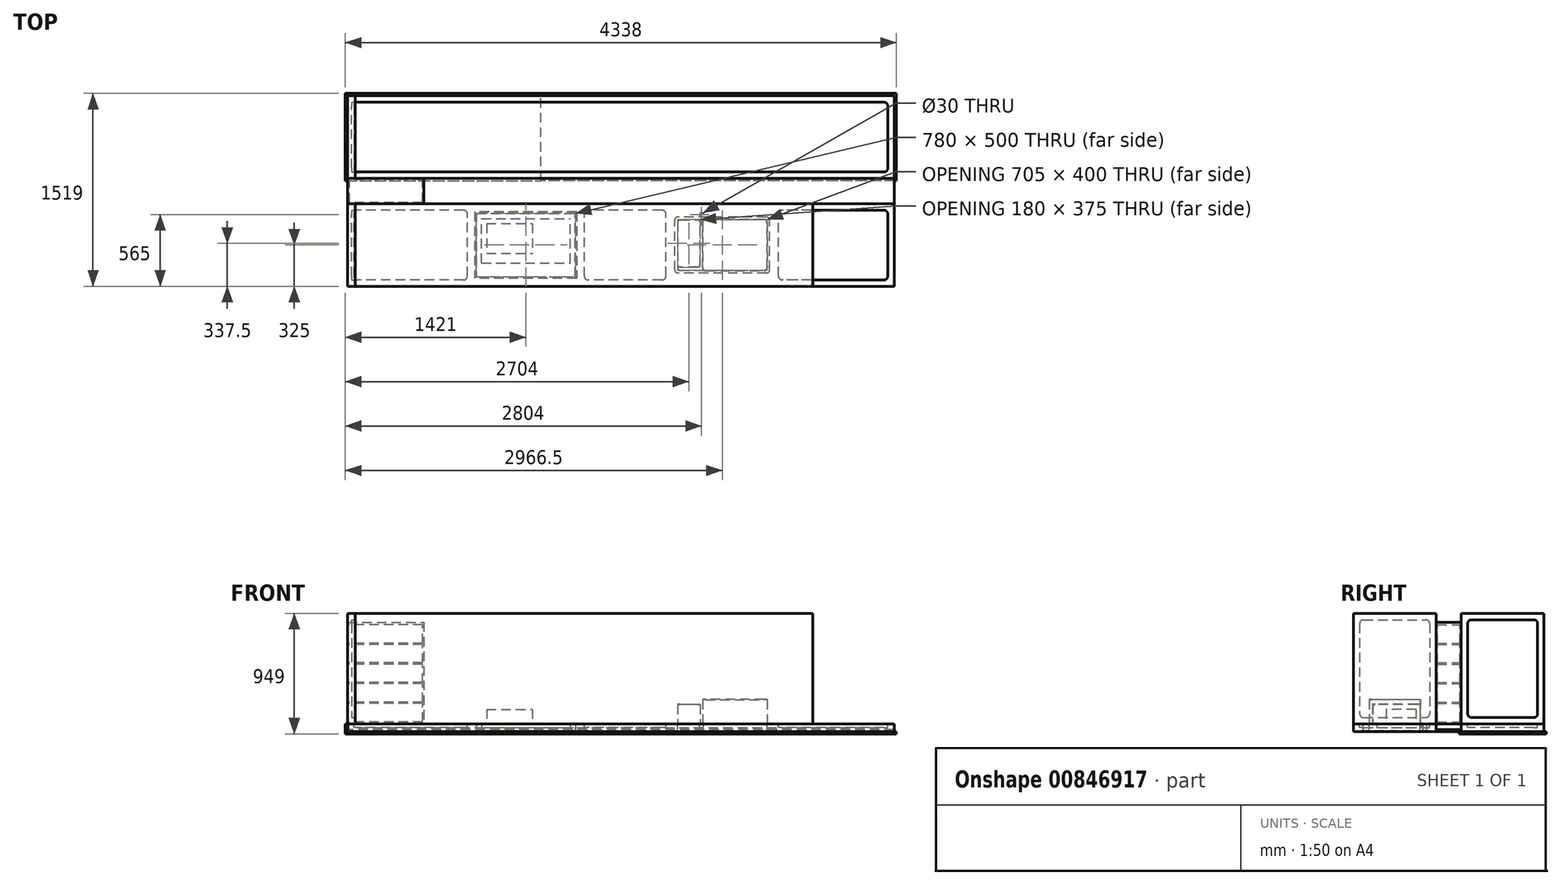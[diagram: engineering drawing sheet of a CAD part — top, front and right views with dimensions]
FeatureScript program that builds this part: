
annotation { "Feature Type Name" : "Feature", "Feature Type Description" : "" }
export const myFeature = defineFeature(function(context is Context, id is Id, definition is map)
    precondition{}
    {
        {
            var Q0;
            Q0=qCreatedBy(makeId("Top.planeOp"),FACE);
            var sketch = newSketch(context, id + "F0", { "sketchPlane" : qUnion([Q0])});
            skLineSegment(sketch, "E0.bottom", {"start": v(0, 0) * mm, "end": v(4300, 0) * mm});
            skLineSegment(sketch, "E0.top", {"start": v(0, 650) * mm, "end": v(4300, 650) * mm});
            skLineSegment(sketch, "E0.left", {"start": v(0, 0) * mm, "end": v(0, 650) * mm});
            skLineSegment(sketch, "E0.right", {"start": v(4300, 0) * mm, "end": v(4300, 650) * mm});
            skSolve(sketch);
        }
        {
            var Q0;
            Q0=makeQuery(id+"F0.imprint","IMPRINT",FACE,{"disambiguationData":[TD([[makeQuery(id+"F0.imprint","IMPRINT",EDGE,{"derivedFrom":sQuery(id+"F0.wireOp",EDGE,"E0.bottom")}),1.0]])]});
            extrude(context, id + "F1", {"entities" : qUnion([Q0]), "depth" : 60 * mm, "offsetDistance" : 25 * mm});
        }
        {
            var Q0;
            Q0=makeQuery(id+"F1.opExtrude","CAP_FACE",FACE,{"disambiguationData":[OSD([sQuery(id+"F0.wireOp",EDGE,"E0.bottom"),sQuery(id+"F0.wireOp",EDGE,"E0.top"),sQuery(id+"F0.wireOp",EDGE,"E0.left"),sQuery(id+"F0.wireOp",EDGE,"E0.right")])],"isStart":false});
            var sketch = newSketch(context, id + "F2", { "sketchPlane" : qUnion([Q0])});
            skLineSegment(sketch, "E1.bottom", {"start": v(2617, 525) * mm, "end": v(3278, 525) * mm});
            skLineSegment(sketch, "E1.top", {"start": v(2617, 125) * mm, "end": v(3278, 125) * mm});
            skLineSegment(sketch, "E1.left", {"start": v(2595, 503) * mm, "end": v(2595, 147) * mm});
            skLineSegment(sketch, "E1.right", {"start": v(3300, 503) * mm, "end": v(3300, 147) * mm});
            skPoint(sketch, "E2.visualSharp", {"position": v(2595, 525) * mm});
            skArc(sketch, "E2.filletArc", {"start": v(2617, 525) * mm, "mid": v(2601.44, 518.56) * mm, "end": v(2595, 503) * mm});
            skPoint(sketch, "E3.visualSharp", {"position": v(3300, 525) * mm});
            skArc(sketch, "E3.filletArc", {"start": v(3300, 503) * mm, "mid": v(3293.56, 518.56) * mm, "end": v(3278, 525) * mm});
            skPoint(sketch, "E4.visualSharp", {"position": v(3300, 125) * mm});
            skArc(sketch, "E4.filletArc", {"start": v(3278, 125) * mm, "mid": v(3293.56, 131.44) * mm, "end": v(3300, 147) * mm});
            skPoint(sketch, "E5.visualSharp", {"position": v(2595, 125) * mm});
            skArc(sketch, "E5.filletArc", {"start": v(2595, 147) * mm, "mid": v(2601.44, 131.44) * mm, "end": v(2617, 125) * mm});
            skCircle(sketch, "E6", {"center": v(2785, 565) * mm, "radius": 15 * mm});
            skSolve(sketch);
        }
        {
            var Q0;
            Q0 = qSketchRegion(id + "F2", true);
            extrude(context, id + "F3", {"entities" : qUnion([Q0]), "operationType" : NewBodyOperationType.REMOVE, "endBound" : BoundingType.THROUGH_ALL, "oppositeDirection" : true, "depth" : 25 * mm, "offsetDistance" : 25 * mm});
        }
        {
            var Q0;
            Q0=makeQuery(id+"F1.opExtrude","CAP_FACE",FACE,{"disambiguationData":[OSD([sQuery(id+"F0.wireOp",EDGE,"E0.bottom"),sQuery(id+"F0.wireOp",EDGE,"E0.top"),sQuery(id+"F0.wireOp",EDGE,"E0.left"),sQuery(id+"F0.wireOp",EDGE,"E0.right")])],"isStart":false});
            var sketch = newSketch(context, id + "F4", { "sketchPlane" : qUnion([Q0])});
            skLineSegment(sketch, "E7.bottom", {"start": v(3298, 105) * mm, "end": v(2597, 105) * mm});
            skLineSegment(sketch, "E7.top", {"start": v(3298, 545) * mm, "end": v(2597, 545) * mm});
            skLineSegment(sketch, "E7.left", {"start": v(3320, 127) * mm, "end": v(3320, 523) * mm});
            skLineSegment(sketch, "E7.right", {"start": v(2575, 127) * mm, "end": v(2575, 523) * mm});
            skPoint(sketch, "E8.visualSharp", {"position": v(2575, 105) * mm});
            skArc(sketch, "E8.filletArc", {"start": v(2575, 127) * mm, "mid": v(2581.44, 111.44) * mm, "end": v(2597, 105) * mm});
            skPoint(sketch, "E9.visualSharp", {"position": v(2575, 545) * mm});
            skArc(sketch, "E9.filletArc", {"start": v(2597, 545) * mm, "mid": v(2581.44, 538.56) * mm, "end": v(2575, 523) * mm});
            skPoint(sketch, "E10.visualSharp", {"position": v(3320, 545) * mm});
            skArc(sketch, "E10.filletArc", {"start": v(3320, 523) * mm, "mid": v(3313.56, 538.56) * mm, "end": v(3298, 545) * mm});
            skPoint(sketch, "E11.visualSharp", {"position": v(3320, 105) * mm});
            skArc(sketch, "E11.filletArc", {"start": v(3298, 105) * mm, "mid": v(3313.56, 111.44) * mm, "end": v(3320, 127) * mm});
            skLineSegment(sketch, "E12.left", {"start": v(2795, 147) * mm, "end": v(2795, 503) * mm});
            skLineSegment(sketch, "E12.right", {"start": v(2775, 172) * mm, "end": v(2775, 503) * mm});
            skLineSegment(sketch, "E13.bottom", {"start": v(2817, 125) * mm, "end": v(3278, 125) * mm});
            skLineSegment(sketch, "E13.top", {"start": v(2817, 525) * mm, "end": v(3278, 525) * mm});
            skLineSegment(sketch, "E13.right", {"start": v(3300, 147) * mm, "end": v(3300, 503) * mm});
            skPoint(sketch, "E14.visualSharp", {"position": v(2795, 125) * mm});
            skArc(sketch, "E14.filletArc", {"start": v(2795, 147) * mm, "mid": v(2801.44, 131.44) * mm, "end": v(2817, 125) * mm});
            skPoint(sketch, "E15.visualSharp", {"position": v(3300, 125) * mm});
            skArc(sketch, "E15.filletArc", {"start": v(3278, 125) * mm, "mid": v(3293.56, 131.44) * mm, "end": v(3300, 147) * mm});
            skPoint(sketch, "E16.visualSharp", {"position": v(3300, 525) * mm});
            skArc(sketch, "E16.filletArc", {"start": v(3300, 503) * mm, "mid": v(3293.56, 518.56) * mm, "end": v(3278, 525) * mm});
            skPoint(sketch, "E17.visualSharp", {"position": v(2795, 525) * mm});
            skArc(sketch, "E17.filletArc", {"start": v(2817, 525) * mm, "mid": v(2801.44, 518.56) * mm, "end": v(2795, 503) * mm});
            skLineSegment(sketch, "E18.bottom", {"start": v(2753, 150) * mm, "end": v(2617, 150) * mm});
            skLineSegment(sketch, "E18.top", {"start": v(2753, 525) * mm, "end": v(2617, 525) * mm});
            skLineSegment(sketch, "E18.right", {"start": v(2595, 172) * mm, "end": v(2595, 503) * mm});
            skPoint(sketch, "E19.visualSharp", {"position": v(2775, 150) * mm});
            skArc(sketch, "E19.filletArc", {"start": v(2753, 150) * mm, "mid": v(2768.56, 156.44) * mm, "end": v(2775, 172) * mm});
            skPoint(sketch, "E20.visualSharp", {"position": v(2595, 525) * mm});
            skArc(sketch, "E20.filletArc", {"start": v(2617, 525) * mm, "mid": v(2601.44, 518.56) * mm, "end": v(2595, 503) * mm});
            skPoint(sketch, "E21.visualSharp", {"position": v(2775, 525) * mm});
            skArc(sketch, "E21.filletArc", {"start": v(2775, 503) * mm, "mid": v(2768.56, 518.56) * mm, "end": v(2753, 525) * mm});
            skPoint(sketch, "E22.visualSharp", {"position": v(2595, 150) * mm});
            skArc(sketch, "E22.filletArc", {"start": v(2595, 172) * mm, "mid": v(2601.44, 156.44) * mm, "end": v(2617, 150) * mm});
            skSolve(sketch);
        }
        {
            var Q0;
            Q0 = qSketchRegion(id + "F4", true);
            extrude(context, id + "F5", {"entities" : qUnion([Q0]), "depth" : 2 * mm, "offsetDistance" : 25 * mm});
        }
        {
            var Q0;
            Q0=makeQuery(id+"F5.opExtrude","CAP_FACE",FACE,{"disambiguationData":[OSD([sQuery(id+"F4.wireOp",EDGE,"E7.bottom"),sQuery(id+"F4.wireOp",EDGE,"E7.top"),sQuery(id+"F4.wireOp",EDGE,"E7.left"),sQuery(id+"F4.wireOp",EDGE,"E7.right"),sQuery(id+"F4.wireOp",EDGE,"E8.filletArc"),sQuery(id+"F4.wireOp",EDGE,"E9.filletArc"),sQuery(id+"F4.wireOp",EDGE,"E10.filletArc"),sQuery(id+"F4.wireOp",EDGE,"E11.filletArc"),sQuery(id+"F4.wireOp",EDGE,"E13.bottom"),sQuery(id+"F4.wireOp",EDGE,"E13.top"),sQuery(id+"F4.wireOp",EDGE,"E12.left"),sQuery(id+"F4.wireOp",EDGE,"E13.right"),sQuery(id+"F4.wireOp",EDGE,"E14.filletArc"),sQuery(id+"F4.wireOp",EDGE,"E15.filletArc"),sQuery(id+"F4.wireOp",EDGE,"E16.filletArc"),sQuery(id+"F4.wireOp",EDGE,"E17.filletArc"),sQuery(id+"F4.wireOp",EDGE,"E18.bottom"),sQuery(id+"F4.wireOp",EDGE,"E18.top"),sQuery(id+"F4.wireOp",EDGE,"E12.right"),sQuery(id+"F4.wireOp",EDGE,"E18.right"),sQuery(id+"F4.wireOp",EDGE,"E19.filletArc"),sQuery(id+"F4.wireOp",EDGE,"E20.filletArc"),sQuery(id+"F4.wireOp",EDGE,"E21.filletArc"),sQuery(id+"F4.wireOp",EDGE,"E22.filletArc")])],"isStart":false});
            var sketch = newSketch(context, id + "F6", { "sketchPlane" : qUnion([Q0])});
            skLineSegment(sketch, "E23.0.0", {"start": v(3278, 525) * mm, "end": v(2817, 525) * mm});
            skArc(sketch, "E23.0.1", {"start": v(2817, 525) * mm, "mid": v(2801.44, 518.56) * mm, "end": v(2795, 503) * mm});
            skLineSegment(sketch, "E23.0.2", {"start": v(2795, 503) * mm, "end": v(2795, 147) * mm});
            skArc(sketch, "E23.0.3", {"start": v(2795, 147) * mm, "mid": v(2801.44, 131.44) * mm, "end": v(2817, 125) * mm});
            skLineSegment(sketch, "E23.0.4", {"start": v(2817, 125) * mm, "end": v(3278, 125) * mm});
            skArc(sketch, "E23.0.5", {"start": v(3278, 125) * mm, "mid": v(3293.56, 131.44) * mm, "end": v(3300, 147) * mm});
            skLineSegment(sketch, "E23.0.6", {"start": v(3300, 147) * mm, "end": v(3300, 503) * mm});
            skArc(sketch, "E23.0.7", {"start": v(3300, 503) * mm, "mid": v(3293.56, 518.56) * mm, "end": v(3278, 525) * mm});
            skArc(sketch, "E24.0", {"start": v(3302, 503) * mm, "mid": v(3294.97, 519.97) * mm, "end": v(3278, 527) * mm});
            skLineSegment(sketch, "E24.1", {"start": v(3302, 147) * mm, "end": v(3302, 503) * mm});
            skLineSegment(sketch, "E24.2", {"start": v(3278, 527) * mm, "end": v(2817, 527) * mm});
            skArc(sketch, "E24.3", {"start": v(3278, 123) * mm, "mid": v(3294.97, 130.03) * mm, "end": v(3302, 147) * mm});
            skArc(sketch, "E24.4", {"start": v(2817, 527) * mm, "mid": v(2800.03, 519.97) * mm, "end": v(2793, 503) * mm});
            skLineSegment(sketch, "E24.5", {"start": v(2793, 503) * mm, "end": v(2793, 147) * mm});
            skArc(sketch, "E24.6", {"start": v(2793, 147) * mm, "mid": v(2800.03, 130.03) * mm, "end": v(2817, 123) * mm});
            skLineSegment(sketch, "E24.7", {"start": v(2817, 123) * mm, "end": v(3278, 123) * mm});
            skSolve(sketch);
        }
        {
            var Q0;
            Q0 = qSketchRegion(id + "F6", true);
            extrude(context, id + "F7", {"entities" : qUnion([Q0]), "operationType" : NewBodyOperationType.ADD, "depth" : 190 * mm, "offsetDistance" : 25 * mm});
        }
        {
            var Q0;
            Q0=makeQuery(id+"F7.opExtrude","CAP_FACE",FACE,{"disambiguationData":[OSD([sQuery(id+"F6.wireOp",EDGE,"E23.0.0"),sQuery(id+"F6.wireOp",EDGE,"E23.0.1"),sQuery(id+"F6.wireOp",EDGE,"E23.0.2"),sQuery(id+"F6.wireOp",EDGE,"E23.0.3"),sQuery(id+"F6.wireOp",EDGE,"E23.0.4"),sQuery(id+"F6.wireOp",EDGE,"E23.0.5"),sQuery(id+"F6.wireOp",EDGE,"E23.0.6"),sQuery(id+"F6.wireOp",EDGE,"E23.0.7"),sQuery(id+"F6.wireOp",EDGE,"E24.0"),sQuery(id+"F6.wireOp",EDGE,"E24.1"),sQuery(id+"F6.wireOp",EDGE,"E24.2"),sQuery(id+"F6.wireOp",EDGE,"E24.3"),sQuery(id+"F6.wireOp",EDGE,"E24.4"),sQuery(id+"F6.wireOp",EDGE,"E24.5"),sQuery(id+"F6.wireOp",EDGE,"E24.6"),sQuery(id+"F6.wireOp",EDGE,"E24.7")])],"isStart":false});
            var sketch = newSketch(context, id + "F8", { "sketchPlane" : qUnion([Q0])});
            skLineSegment(sketch, "E25.0.0", {"start": v(3278, 525) * mm, "end": v(2817, 525) * mm});
            skArc(sketch, "E25.0.1", {"start": v(2817, 525) * mm, "mid": v(2801.44, 518.56) * mm, "end": v(2795, 503) * mm});
            skLineSegment(sketch, "E25.0.2", {"start": v(2795, 503) * mm, "end": v(2795, 147) * mm});
            skArc(sketch, "E25.0.3", {"start": v(2795, 147) * mm, "mid": v(2801.44, 131.44) * mm, "end": v(2817, 125) * mm});
            skLineSegment(sketch, "E25.0.4", {"start": v(2817, 125) * mm, "end": v(3278, 125) * mm});
            skArc(sketch, "E25.0.5", {"start": v(3278, 125) * mm, "mid": v(3293.56, 131.44) * mm, "end": v(3300, 147) * mm});
            skLineSegment(sketch, "E25.0.6", {"start": v(3300, 147) * mm, "end": v(3300, 503) * mm});
            skArc(sketch, "E25.0.7", {"start": v(3300, 503) * mm, "mid": v(3293.56, 518.56) * mm, "end": v(3278, 525) * mm});
            skSolve(sketch);
        }
        {
            var Q0;
            Q0 = qSketchRegion(id + "F8", true);
            extrude(context, id + "F9", {"entities" : qUnion([Q0]), "operationType" : NewBodyOperationType.ADD, "oppositeDirection" : true, "depth" : 2 * mm, "offsetDistance" : 25 * mm});
        }
        {
            var Q0;
            Q0=makeQuery(id+"F5.opExtrude","CAP_FACE",FACE,{"disambiguationData":[OSD([sQuery(id+"F4.wireOp",EDGE,"E7.bottom"),sQuery(id+"F4.wireOp",EDGE,"E7.top"),sQuery(id+"F4.wireOp",EDGE,"E7.left"),sQuery(id+"F4.wireOp",EDGE,"E7.right"),sQuery(id+"F4.wireOp",EDGE,"E8.filletArc"),sQuery(id+"F4.wireOp",EDGE,"E9.filletArc"),sQuery(id+"F4.wireOp",EDGE,"E10.filletArc"),sQuery(id+"F4.wireOp",EDGE,"E11.filletArc"),sQuery(id+"F4.wireOp",EDGE,"E13.bottom"),sQuery(id+"F4.wireOp",EDGE,"E13.top"),sQuery(id+"F4.wireOp",EDGE,"E12.left"),sQuery(id+"F4.wireOp",EDGE,"E13.right"),sQuery(id+"F4.wireOp",EDGE,"E14.filletArc"),sQuery(id+"F4.wireOp",EDGE,"E15.filletArc"),sQuery(id+"F4.wireOp",EDGE,"E16.filletArc"),sQuery(id+"F4.wireOp",EDGE,"E17.filletArc"),sQuery(id+"F4.wireOp",EDGE,"E18.bottom"),sQuery(id+"F4.wireOp",EDGE,"E18.top"),sQuery(id+"F4.wireOp",EDGE,"E12.right"),sQuery(id+"F4.wireOp",EDGE,"E18.right"),sQuery(id+"F4.wireOp",EDGE,"E19.filletArc"),sQuery(id+"F4.wireOp",EDGE,"E20.filletArc"),sQuery(id+"F4.wireOp",EDGE,"E21.filletArc"),sQuery(id+"F4.wireOp",EDGE,"E22.filletArc")])],"isStart":false});
            var sketch = newSketch(context, id + "F10", { "sketchPlane" : qUnion([Q0])});
            skLineSegment(sketch, "E26.0", {"start": v(2753, 152) * mm, "end": v(2617, 152) * mm});
            skArc(sketch, "E26.1", {"start": v(2597, 172) * mm, "mid": v(2602.86, 157.86) * mm, "end": v(2617, 152) * mm});
            skArc(sketch, "E26.2", {"start": v(2753, 152) * mm, "mid": v(2767.14, 157.86) * mm, "end": v(2773, 172) * mm});
            skLineSegment(sketch, "E26.3", {"start": v(2597, 503) * mm, "end": v(2597, 172) * mm});
            skLineSegment(sketch, "E26.4", {"start": v(2773, 172) * mm, "end": v(2773, 503) * mm});
            skArc(sketch, "E26.5", {"start": v(2773, 503) * mm, "mid": v(2767.14, 517.14) * mm, "end": v(2753, 523) * mm});
            skLineSegment(sketch, "E26.6", {"start": v(2617, 523) * mm, "end": v(2753, 523) * mm});
            skArc(sketch, "E26.7", {"start": v(2617, 523) * mm, "mid": v(2602.86, 517.14) * mm, "end": v(2597, 503) * mm});
            skArc(sketch, "E27.0", {"start": v(2595, 172) * mm, "mid": v(2601.44, 156.44) * mm, "end": v(2617, 150) * mm});
            skLineSegment(sketch, "E28.0", {"start": v(2753, 150) * mm, "end": v(2617, 150) * mm});
            skArc(sketch, "E29.0", {"start": v(2753, 150) * mm, "mid": v(2768.56, 156.44) * mm, "end": v(2775, 172) * mm});
            skLineSegment(sketch, "E30.0", {"start": v(2775, 172) * mm, "end": v(2775, 503) * mm});
            skArc(sketch, "E31.0", {"start": v(2775, 503) * mm, "mid": v(2768.56, 518.56) * mm, "end": v(2753, 525) * mm});
            skLineSegment(sketch, "E32.0", {"start": v(2617, 525) * mm, "end": v(2753, 525) * mm});
            skArc(sketch, "E33.0", {"start": v(2617, 525) * mm, "mid": v(2601.44, 518.56) * mm, "end": v(2595, 503) * mm});
            skLineSegment(sketch, "E34.0", {"start": v(2595, 503) * mm, "end": v(2595, 172) * mm});
            skSolve(sketch);
        }
        {
            var Q0;
            Q0=makeQuery(id+"F10.imprint","IMPRINT",FACE,{"disambiguationData":[TD([[makeQuery(id+"F10.imprint","IMPRINT",EDGE,{"derivedFrom":sQuery(id+"F10.wireOp",EDGE,"E26.0")}),1.0]])]});
            extrude(context, id + "F11", {"entities" : qUnion([Q0]), "operationType" : NewBodyOperationType.ADD, "depth" : 150 * mm, "offsetDistance" : 25 * mm});
        }
        {
            var Q0;
            {var subQ0=sQuery(id+"F0.wireOp",EDGE,"E0.bottom");var subQ1=sQuery(id+"F0.wireOp",EDGE,"E0.left");var subQ2=sQuery(id+"F0.wireOp",EDGE,"E0.right");Q0=makeQuery(id+"F5oApF7oSFTbvsd_1.boolean.opBoolean","SPLIT",FACE,{"disambiguationData":[TD([makeQuery(id+"F1.opExtrude","SWEPT_FACE",FACE,{"disambiguationData":[OSD([subQ0])]})])],"derivedFrom":makeQuery(id+"F1.opExtrude","CAP_FACE",FACE,{"disambiguationData":[OSD([subQ0,sQuery(id+"F0.wireOp",EDGE,"E0.top"),subQ1,subQ2])],"isStart":true})});}
            var sketch = newSketch(context, id + "F12", { "sketchPlane" : qUnion([Q0])});
            skLineSegment(sketch, "E35.bottom", {"start": v(1804, -587) * mm, "end": v(1000, -587) * mm});
            skLineSegment(sketch, "E35.top", {"start": v(1804, -63) * mm, "end": v(1000, -63) * mm});
            skLineSegment(sketch, "E35.left", {"start": v(1804, -587) * mm, "end": v(1804, -63) * mm});
            skLineSegment(sketch, "E35.right", {"start": v(1000, -587) * mm, "end": v(1000, -63) * mm});
            skSolve(sketch);
        }
        {
            var Q0;
            Q0=makeQuery(id+"F12.imprint","IMPRINT",FACE,{"disambiguationData":[TD([[makeQuery(id+"F12.imprint","IMPRINT",EDGE,{"derivedFrom":sQuery(id+"F12.wireOp",EDGE,"E35.bottom")}),-1.0]])]});
            extrude(context, id + "F13", {"entities" : qUnion([Q0]), "operationType" : NewBodyOperationType.REMOVE, "oppositeDirection" : true, "depth" : 5 * mm, "offsetDistance" : 25 * mm});
        }
        {
            var Q0;
            Q0=makeQuery(id+"F13.boolean.opBoolean","COPY",FACE,{"derivedFrom":makeQuery(id+"F13.opExtrude","CAP_FACE",FACE,{"disambiguationData":[OSD([sQuery(id+"F12.wireOp",EDGE,"E35.bottom"),sQuery(id+"F12.wireOp",EDGE,"E35.top"),sQuery(id+"F12.wireOp",EDGE,"E35.left"),sQuery(id+"F12.wireOp",EDGE,"E35.right")])],"isStart":false})});
            var sketch = newSketch(context, id + "F14", { "sketchPlane" : qUnion([Q0])});
            skLineSegment(sketch, "E36.0", {"start": v(1792, -575) * mm, "end": v(1792, -75) * mm});
            skLineSegment(sketch, "E36.1", {"start": v(1012, -575) * mm, "end": v(1792, -575) * mm});
            skLineSegment(sketch, "E36.2", {"start": v(1012, -75) * mm, "end": v(1012, -575) * mm});
            skLineSegment(sketch, "E36.3", {"start": v(1792, -75) * mm, "end": v(1012, -75) * mm});
            skSolve(sketch);
        }
        {
            var Q0;
            Q0=makeQuery(id+"F14.imprint","IMPRINT",FACE,{"disambiguationData":[TD([[makeQuery(id+"F14.imprint","IMPRINT",EDGE,{"derivedFrom":sQuery(id+"F14.wireOp",EDGE,"E36.0")}),1.0]])]});
            extrude(context, id + "F15", {"entities" : qUnion([Q0]), "operationType" : NewBodyOperationType.REMOVE, "endBound" : BoundingType.THROUGH_ALL, "oppositeDirection" : true, "depth" : 25 * mm, "offsetDistance" : 25 * mm});
        }
        {
            var Q0;
            {var subQ0=sQuery(id+"F0.wireOp",EDGE,"E0.bottom");var subQ1=sQuery(id+"F0.wireOp",EDGE,"E0.left");var subQ2=sQuery(id+"F0.wireOp",EDGE,"E0.right");Q0=makeQuery(id+"F5oApF7oSFTbvsd_1.boolean.opBoolean","SPLIT",FACE,{"disambiguationData":[TD([makeQuery(id+"F1.opExtrude","SWEPT_FACE",FACE,{"disambiguationData":[OSD([subQ0])]})])],"derivedFrom":makeQuery(id+"F1.opExtrude","CAP_FACE",FACE,{"disambiguationData":[OSD([subQ0,sQuery(id+"F0.wireOp",EDGE,"E0.top"),subQ1,subQ2])],"isStart":true})});}
            var sketch = newSketch(context, id + "F16", { "sketchPlane" : qUnion([Q0])});
            skLineSegment(sketch, "E37.bottom", {"start": v(1802, -585) * mm, "end": v(1002, -585) * mm});
            skLineSegment(sketch, "E37.top", {"start": v(1802, -65) * mm, "end": v(1002, -65) * mm});
            skLineSegment(sketch, "E37.left", {"start": v(1802, -585) * mm, "end": v(1802, -65) * mm});
            skLineSegment(sketch, "E37.right", {"start": v(1002, -585) * mm, "end": v(1002, -65) * mm});
            skSolve(sketch);
        }
        {
            var Q0;
            Q0 = qSketchRegion(id + "F16", true);
            extrude(context, id + "F17", {"entities" : qUnion([Q0]), "oppositeDirection" : true, "depth" : 5 * mm, "offsetDistance" : 25 * mm});
        }
        {
            var Q0;
            Q0=makeQuery(id+"F17.opExtrude","CAP_FACE",FACE,{"disambiguationData":[OSD([sQuery(id+"F16.wireOp",EDGE,"E37.bottom"),sQuery(id+"F16.wireOp",EDGE,"E37.top"),sQuery(id+"F16.wireOp",EDGE,"E37.left"),sQuery(id+"F16.wireOp",EDGE,"E37.right")])],"isStart":false});
            var sketch = newSketch(context, id + "F18", { "sketchPlane" : qUnion([Q0])});
            skLineSegment(sketch, "E38.bottom", {"start": v(1013.5, 76.5) * mm, "end": v(1790.5, 76.5) * mm});
            skLineSegment(sketch, "E38.top", {"start": v(1013.5, 573.5) * mm, "end": v(1790.5, 573.5) * mm});
            skLineSegment(sketch, "E38.left", {"start": v(1013.5, 76.5) * mm, "end": v(1013.5, 573.5) * mm});
            skLineSegment(sketch, "E38.right", {"start": v(1790.5, 76.5) * mm, "end": v(1790.5, 573.5) * mm});
            skLineSegment(sketch, "E39", {"start": v(1121.78, 65) * mm, "end": v(1121.78, 76.5) * mm, "construction": true});
            skLineSegment(sketch, "E40", {"start": v(1128.6, 573.5) * mm, "end": v(1128.6, 585) * mm, "construction": true});
            skLineSegment(sketch, "E41", {"start": v(1002, 297.1) * mm, "end": v(1013.5, 297.1) * mm, "construction": true});
            skLineSegment(sketch, "E42", {"start": v(1802, 255.84) * mm, "end": v(1790.5, 255.84) * mm, "construction": true});
            skSolve(sketch);
        }
        {
            var Q0;
            Q0=makeQuery(id+"F18.imprint","IMPRINT",FACE,{"disambiguationData":[TD([[makeQuery(id+"F18.imprint","IMPRINT",EDGE,{"derivedFrom":sQuery(id+"F18.wireOp",EDGE,"E38.bottom")}),1.0]])]});
            extrude(context, id + "F19", {"entities" : qUnion([Q0]), "operationType" : NewBodyOperationType.ADD, "depth" : 25 * mm, "offsetDistance" : 25 * mm});
        }
        {
            var Q0;
            Q0=makeQuery(id+"F19.opExtrude","CAP_FACE",FACE,{"disambiguationData":[OSD([sQuery(id+"F18.wireOp",EDGE,"E38.bottom"),sQuery(id+"F18.wireOp",EDGE,"E38.top"),sQuery(id+"F18.wireOp",EDGE,"E38.left"),sQuery(id+"F18.wireOp",EDGE,"E38.right")])],"isStart":false});
            var sketch = newSketch(context, id + "F20", { "sketchPlane" : qUnion([Q0])});
            skLineSegment(sketch, "E43.bottom", {"start": v(1053.5, 183.5) * mm, "end": v(1753.5, 183.5) * mm});
            skLineSegment(sketch, "E43.top", {"start": v(1053.5, 533.5) * mm, "end": v(1753.5, 533.5) * mm});
            skLineSegment(sketch, "E43.left", {"start": v(1053.5, 183.5) * mm, "end": v(1053.5, 533.5) * mm});
            skLineSegment(sketch, "E43.right", {"start": v(1753.5, 183.5) * mm, "end": v(1753.5, 533.5) * mm});
            skSolve(sketch);
        }
        {
            var Q0;
            Q0=makeQuery(id+"F20.imprint","IMPRINT",FACE,{"disambiguationData":[TD([[makeQuery(id+"F20.imprint","IMPRINT",EDGE,{"derivedFrom":sQuery(id+"F20.wireOp",EDGE,"E43.bottom")}),1.0]])]});
            extrude(context, id + "F21", {"entities" : qUnion([Q0]), "operationType" : NewBodyOperationType.ADD, "depth" : 25 * mm, "offsetDistance" : 25 * mm});
        }
        {
            var Q0;
            Q0=makeQuery(id+"F21.opExtrude","CAP_FACE",FACE,{"disambiguationData":[OSD([sQuery(id+"F20.wireOp",EDGE,"E43.bottom"),sQuery(id+"F20.wireOp",EDGE,"E43.top"),sQuery(id+"F20.wireOp",EDGE,"E43.left"),sQuery(id+"F20.wireOp",EDGE,"E43.right")])],"isStart":false});
            var sketch = newSketch(context, id + "F22", { "sketchPlane" : qUnion([Q0])});
            skLineSegment(sketch, "E44.bottom", {"start": v(1093.5, 493.5) * mm, "end": v(1453.5, 493.5) * mm});
            skLineSegment(sketch, "E44.top", {"start": v(1093.5, 258.5) * mm, "end": v(1453.5, 258.5) * mm});
            skLineSegment(sketch, "E44.left", {"start": v(1093.5, 493.5) * mm, "end": v(1093.5, 258.5) * mm});
            skLineSegment(sketch, "E44.right", {"start": v(1453.5, 493.5) * mm, "end": v(1453.5, 258.5) * mm});
            skSolve(sketch);
        }
        {
            var Q0;
            Q0=makeQuery(id+"F22.imprint","IMPRINT",FACE,{"disambiguationData":[TD([[makeQuery(id+"F22.imprint","IMPRINT",EDGE,{"derivedFrom":sQuery(id+"F22.wireOp",EDGE,"E44.bottom")}),-1.0]])]});
            extrude(context, id + "F23", {"entities" : qUnion([Q0]), "operationType" : NewBodyOperationType.ADD, "depth" : 120 * mm, "offsetDistance" : 25 * mm});
        }
        {
            var Q0;
            Q0=makeQuery(id+"F11.opExtrude","CAP_FACE",FACE,{"disambiguationData":[OSD([sQuery(id+"F10.wireOp",EDGE,"E26.0"),sQuery(id+"F10.wireOp",EDGE,"E26.1"),sQuery(id+"F10.wireOp",EDGE,"E26.2"),sQuery(id+"F10.wireOp",EDGE,"E26.3"),sQuery(id+"F10.wireOp",EDGE,"E26.4"),sQuery(id+"F10.wireOp",EDGE,"E26.5"),sQuery(id+"F10.wireOp",EDGE,"E26.6"),sQuery(id+"F10.wireOp",EDGE,"E26.7"),sQuery(id+"F10.wireOp",EDGE,"E27.0"),sQuery(id+"F10.wireOp",EDGE,"E28.0"),sQuery(id+"F10.wireOp",EDGE,"E29.0"),sQuery(id+"F10.wireOp",EDGE,"E30.0"),sQuery(id+"F10.wireOp",EDGE,"E31.0"),sQuery(id+"F10.wireOp",EDGE,"E32.0"),sQuery(id+"F10.wireOp",EDGE,"E33.0"),sQuery(id+"F10.wireOp",EDGE,"E34.0")])],"isStart":false});
            var sketch = newSketch(context, id + "F24", { "sketchPlane" : qUnion([Q0])});
            skSolve(sketch);
        }
        {
            var Q0;
            Q0=makeQuery(id+"F24.imprint","IMPRINT",FACE,{"disambiguationData":[TD([[makeQuery(id+"F24.imprint","IMPRINT",EDGE,{"derivedFrom":makeQuery(id+"F11.opExtrude","CAP_EDGE",EDGE,{"disambiguationData":[OSD([sQuery(id+"F10.wireOp",EDGE,"E26.0")])],"isStart":false})}),1.0]])]});
            var sketch = newSketch(context, id + "F25", { "sketchPlane" : qUnion([Q0])});
            skArc(sketch, "E45.0", {"start": v(2753, 150) * mm, "mid": v(2768.56, 156.44) * mm, "end": v(2775, 172) * mm});
            skLineSegment(sketch, "E46.0", {"start": v(2775, 172) * mm, "end": v(2775, 503) * mm});
            skArc(sketch, "E47.0", {"start": v(2775, 503) * mm, "mid": v(2768.56, 518.56) * mm, "end": v(2753, 525) * mm});
            skLineSegment(sketch, "E48.0", {"start": v(2617, 525) * mm, "end": v(2753, 525) * mm});
            skArc(sketch, "E49.0", {"start": v(2617, 525) * mm, "mid": v(2601.44, 518.56) * mm, "end": v(2595, 503) * mm});
            skLineSegment(sketch, "E50.0", {"start": v(2595, 503) * mm, "end": v(2595, 172) * mm});
            skArc(sketch, "E51.0", {"start": v(2595, 172) * mm, "mid": v(2601.44, 156.44) * mm, "end": v(2617, 150) * mm});
            skLineSegment(sketch, "E52.0", {"start": v(2753, 150) * mm, "end": v(2617, 150) * mm});
            skSolve(sketch);
        }
        {
            var Q0;
            Q0 = qSketchRegion(id + "F25", true);
            extrude(context, id + "F26", {"entities" : qUnion([Q0]), "operationType" : NewBodyOperationType.ADD, "depth" : 2 * mm, "offsetDistance" : 25 * mm});
        }
        {
            var Q0;
            Q0=makeQuery(id+"F1.opExtrude","CAP_FACE",FACE,{"disambiguationData":[OSD([sQuery(id+"F0.wireOp",EDGE,"E0.bottom"),sQuery(id+"F0.wireOp",EDGE,"E0.top"),sQuery(id+"F0.wireOp",EDGE,"E0.left"),sQuery(id+"F0.wireOp",EDGE,"E0.right")])],"isStart":false});
            var sketch = newSketch(context, id + "F27", { "sketchPlane" : qUnion([Q0])});
            skLineSegment(sketch, "E53.bottom", {"start": v(4220, 50) * mm, "end": v(3420, 50) * mm});
            skLineSegment(sketch, "E53.top", {"start": v(4220, 600) * mm, "end": v(3420, 600) * mm});
            skLineSegment(sketch, "E53.left", {"start": v(4250, 80) * mm, "end": v(4250, 570) * mm});
            skLineSegment(sketch, "E53.right", {"start": v(3390, 80) * mm, "end": v(3390, 570) * mm});
            skLineSegment(sketch, "E54.bottom", {"start": v(2475, 50) * mm, "end": v(1892, 50) * mm});
            skLineSegment(sketch, "E54.top", {"start": v(2475, 600) * mm, "end": v(1892, 600) * mm});
            skLineSegment(sketch, "E54.left", {"start": v(2505, 80) * mm, "end": v(2505, 570) * mm});
            skLineSegment(sketch, "E54.right", {"start": v(1862, 80) * mm, "end": v(1862, 570) * mm});
            skLineSegment(sketch, "E55.bottom", {"start": v(912, 50) * mm, "end": v(80, 50) * mm});
            skLineSegment(sketch, "E55.top", {"start": v(912, 600) * mm, "end": v(80, 600) * mm});
            skLineSegment(sketch, "E55.left", {"start": v(942, 80) * mm, "end": v(942, 570) * mm});
            skLineSegment(sketch, "E55.right", {"start": v(50, 80) * mm, "end": v(50, 570) * mm});
            skPoint(sketch, "E56.visualSharp", {"position": v(50, 600) * mm});
            skArc(sketch, "E56.filletArc", {"start": v(80, 600) * mm, "mid": v(58.79, 591.21) * mm, "end": v(50, 570) * mm});
            skPoint(sketch, "E57.visualSharp", {"position": v(942, 600) * mm});
            skArc(sketch, "E57.filletArc", {"start": v(942, 570) * mm, "mid": v(933.21, 591.21) * mm, "end": v(912, 600) * mm});
            skPoint(sketch, "E58.visualSharp", {"position": v(942, 50) * mm});
            skArc(sketch, "E58.filletArc", {"start": v(912, 50) * mm, "mid": v(933.21, 58.79) * mm, "end": v(942, 80) * mm});
            skPoint(sketch, "E59.visualSharp", {"position": v(50, 50) * mm});
            skArc(sketch, "E59.filletArc", {"start": v(50, 80) * mm, "mid": v(58.79, 58.79) * mm, "end": v(80, 50) * mm});
            skPoint(sketch, "E60.visualSharp", {"position": v(1862, 600) * mm});
            skArc(sketch, "E60.filletArc", {"start": v(1892, 600) * mm, "mid": v(1870.79, 591.21) * mm, "end": v(1862, 570) * mm});
            skPoint(sketch, "E61.visualSharp", {"position": v(2505, 600) * mm});
            skArc(sketch, "E61.filletArc", {"start": v(2505, 570) * mm, "mid": v(2496.21, 591.21) * mm, "end": v(2475, 600) * mm});
            skPoint(sketch, "E62.visualSharp", {"position": v(2505, 50) * mm});
            skArc(sketch, "E62.filletArc", {"start": v(2475, 50) * mm, "mid": v(2496.21, 58.79) * mm, "end": v(2505, 80) * mm});
            skPoint(sketch, "E63.visualSharp", {"position": v(1862, 50) * mm});
            skArc(sketch, "E63.filletArc", {"start": v(1862, 80) * mm, "mid": v(1870.79, 58.79) * mm, "end": v(1892, 50) * mm});
            skPoint(sketch, "E64.visualSharp", {"position": v(4250, 600) * mm});
            skArc(sketch, "E64.filletArc", {"start": v(4250, 570) * mm, "mid": v(4241.21, 591.21) * mm, "end": v(4220, 600) * mm});
            skPoint(sketch, "E65.visualSharp", {"position": v(4250, 50) * mm});
            skArc(sketch, "E65.filletArc", {"start": v(4220, 50) * mm, "mid": v(4241.21, 58.79) * mm, "end": v(4250, 80) * mm});
            skPoint(sketch, "E66.visualSharp", {"position": v(3390, 50) * mm});
            skArc(sketch, "E66.filletArc", {"start": v(3390, 80) * mm, "mid": v(3398.79, 58.79) * mm, "end": v(3420, 50) * mm});
            skPoint(sketch, "E67.visualSharp", {"position": v(3390, 600) * mm});
            skArc(sketch, "E67.filletArc", {"start": v(3420, 600) * mm, "mid": v(3398.79, 591.21) * mm, "end": v(3390, 570) * mm});
            skSolve(sketch);
        }
        {
            var Q0;
            Q0 = qSketchRegion(id + "F27", true);
            extrude(context, id + "F28", {"entities" : qUnion([Q0]), "operationType" : NewBodyOperationType.REMOVE, "oppositeDirection" : true, "depth" : 30 * mm, "offsetDistance" : 25 * mm});
        }
        {
            var Q0;
            Q0 = qSketchRegion(id + "F27", true);
            extrude(context, id + "F29", {"entities" : qUnion([Q0]), "oppositeDirection" : true, "depth" : 30 * mm, "offsetDistance" : 25 * mm});
        }
        {
            var Q0;
            Q0=makeQuery(id+"F1.opExtrude","CAP_FACE",FACE,{"disambiguationData":[OSD([sQuery(id+"F0.wireOp",EDGE,"E0.bottom"),sQuery(id+"F0.wireOp",EDGE,"E0.top"),sQuery(id+"F0.wireOp",EDGE,"E0.left"),sQuery(id+"F0.wireOp",EDGE,"E0.right")])],"isStart":true});
            var sketch = newSketch(context, id + "F30", { "sketchPlane" : qUnion([Q0])});
            skLineSegment(sketch, "E68.bottom", {"start": v(4300, -850) * mm, "end": v(0, -850) * mm});
            skLineSegment(sketch, "E68.top", {"start": v(4300, -1500) * mm, "end": v(0, -1500) * mm});
            skLineSegment(sketch, "E68.left", {"start": v(4300, -850) * mm, "end": v(4300, -1500) * mm});
            skLineSegment(sketch, "E68.right", {"start": v(0, -850) * mm, "end": v(0, -1500) * mm});
            skSolve(sketch);
        }
        {
            var Q0;
            Q0=makeQuery(id+"F30.imprint","IMPRINT",FACE,{"disambiguationData":[TD([[makeQuery(id+"F30.imprint","IMPRINT",EDGE,{"derivedFrom":sQuery(id+"F30.wireOp",EDGE,"E68.bottom")}),1.0]])]});
            extrude(context, id + "F31", {"entities" : qUnion([Q0]), "oppositeDirection" : true, "depth" : 60 * mm, "offsetDistance" : 25 * mm});
        }
        {
            var Q0;
            Q0=makeQuery(id+"F31.opExtrude","CAP_FACE",FACE,{"disambiguationData":[OSD([sQuery(id+"F30.wireOp",EDGE,"E68.bottom"),sQuery(id+"F30.wireOp",EDGE,"E68.top"),sQuery(id+"F30.wireOp",EDGE,"E68.left"),sQuery(id+"F30.wireOp",EDGE,"E68.right")])],"isStart":false});
            var sketch = newSketch(context, id + "F32", { "sketchPlane" : qUnion([Q0])});
            skLineSegment(sketch, "E69.bottom", {"start": v(80, 1450) * mm, "end": v(4220, 1450) * mm});
            skLineSegment(sketch, "E69.top", {"start": v(80, 900) * mm, "end": v(4220, 900) * mm});
            skLineSegment(sketch, "E69.left", {"start": v(50, 1420) * mm, "end": v(50, 930) * mm});
            skLineSegment(sketch, "E69.right", {"start": v(4250, 1420) * mm, "end": v(4250, 930) * mm});
            skPoint(sketch, "E70.visualSharp", {"position": v(50, 1450) * mm});
            skArc(sketch, "E70.filletArc", {"start": v(80, 1450) * mm, "mid": v(58.79, 1441.21) * mm, "end": v(50, 1420) * mm});
            skPoint(sketch, "E71.visualSharp", {"position": v(50, 900) * mm});
            skArc(sketch, "E71.filletArc", {"start": v(50, 930) * mm, "mid": v(58.79, 908.79) * mm, "end": v(80, 900) * mm});
            skPoint(sketch, "E72.visualSharp", {"position": v(4250, 900) * mm});
            skArc(sketch, "E72.filletArc", {"start": v(4220, 900) * mm, "mid": v(4241.21, 908.79) * mm, "end": v(4250, 930) * mm});
            skPoint(sketch, "E73.visualSharp", {"position": v(4250, 1450) * mm});
            skArc(sketch, "E73.filletArc", {"start": v(4250, 1420) * mm, "mid": v(4241.21, 1441.21) * mm, "end": v(4220, 1450) * mm});
            skSolve(sketch);
        }
        {
            var Q0;
            Q0=makeQuery(id+"F32.imprint","IMPRINT",FACE,{"disambiguationData":[TD([[makeQuery(id+"F32.imprint","IMPRINT",EDGE,{"derivedFrom":sQuery(id+"F32.wireOp",EDGE,"E69.bottom")}),-1.0]])]});
            extrude(context, id + "F33", {"entities" : qUnion([Q0]), "operationType" : NewBodyOperationType.REMOVE, "oppositeDirection" : true, "depth" : 30 * mm, "offsetDistance" : 25 * mm});
        }
        {
            var Q0;
            Q0 = qSketchRegion(id + "F32", true);
            extrude(context, id + "F34", {"entities" : qUnion([Q0]), "oppositeDirection" : true, "depth" : 30 * mm, "offsetDistance" : 25 * mm});
        }
        {
            var Q0;
            Q0=makeQuery(id+"F1.opExtrude","SWEPT_FACE",FACE,{"disambiguationData":[OSD([sQuery(id+"F0.wireOp",EDGE,"E0.top")])]});
            var sketch = newSketch(context, id + "F35", { "sketchPlane" : qUnion([Q0])});
            skLineSegment(sketch, "E74", {"start": v(0, 60.87) * mm, "end": v(0, 0) * mm});
            skLineSegment(sketch, "E75", {"start": v(0, 0) * mm, "end": v(-4300, 0) * mm});
            skLineSegment(sketch, "E76", {"start": v(-4300, 0) * mm, "end": v(-4300, 13.5) * mm});
            skLineSegment(sketch, "E77", {"start": v(-4300, 13.5) * mm, "end": v(-13.5, 13.5) * mm});
            skLineSegment(sketch, "E78", {"start": v(-13.5, 13.5) * mm, "end": v(-13.5, 60.87) * mm});
            skLineSegment(sketch, "E79", {"start": v(-13.5, 60.87) * mm, "end": v(0, 60.87) * mm});
            skSolve(sketch);
        }
        {
            var Q0;
            Q0 = qSketchRegion(id + "F35", true);
            extrude(context, id + "F36", {"entities" : qUnion([Q0]), "depth" : 200 * mm, "offsetDistance" : 25 * mm});
        }
        {
            var Q0;
            Q0=makeQuery(id+"F36.opExtrude","CAP_EDGE",EDGE,{"disambiguationData":[OSD([sQuery(id+"F35.wireOp",EDGE,"E75")])],"isStart":false});
            var Q1;
            Q1=makeQuery(id+"F36.opExtrude","CAP_EDGE",EDGE,{"disambiguationData":[OSD([sQuery(id+"F35.wireOp",EDGE,"E74")])],"isStart":false});
            var Q2;
            Q2=makeQuery(id+"F36.opExtrude","SWEPT_EDGE",EDGE,{"disambiguationData":[OSD([sQuery(id+"F35.wireOp",EDGE,"E74"),sQuery(id+"F35.wireOp",EDGE,"E75")])]});
            var Q3;
            Q3=makeQuery(id+"F36.opExtrude","CAP_EDGE",EDGE,{"disambiguationData":[OSD([sQuery(id+"F35.wireOp",EDGE,"E75")])],"isStart":true});
            var Q4;
            Q4=makeQuery(id+"F36.opExtrude","CAP_EDGE",EDGE,{"disambiguationData":[OSD([sQuery(id+"F35.wireOp",EDGE,"E74")])],"isStart":true});
            var Q5;
            Q5=makeQuery(id+"F36.opExtrude","SWEPT_FACE",FACE,{"disambiguationData":[OSD([sQuery(id+"F35.wireOp",EDGE,"E75")])]});
            fillet(context, id + "F37", {"entities" : qUnion([Q0, Q1, Q2, Q3, Q4, Q5]), "radius" : 1 * mm, "tangentPropagation" : true, "allowEdgeOverflow" : false});
        }
        {
            var Q0;
            Q0=makeQuery(id+"F1.opExtrude","CAP_FACE",FACE,{"disambiguationData":[OSD([sQuery(id+"F0.wireOp",EDGE,"E0.bottom"),sQuery(id+"F0.wireOp",EDGE,"E0.top"),sQuery(id+"F0.wireOp",EDGE,"E0.left"),sQuery(id+"F0.wireOp",EDGE,"E0.right")])],"isStart":false});
            var sketch = newSketch(context, id + "F38", { "sketchPlane" : qUnion([Q0])});
            skLineSegment(sketch, "E80.bottom", {"start": v(0, 650) * mm, "end": v(600, 650) * mm});
            skLineSegment(sketch, "E80.top", {"start": v(0, 850) * mm, "end": v(600, 850) * mm});
            skLineSegment(sketch, "E80.left", {"start": v(0, 650) * mm, "end": v(0, 850) * mm});
            skLineSegment(sketch, "E80.right", {"start": v(600, 650) * mm, "end": v(600, 850) * mm});
            skSolve(sketch);
        }
        {
            var Q0;
            Q0=makeQuery(id+"F38.imprint","IMPRINT",FACE,{"disambiguationData":[TD([[makeQuery(id+"F38.imprint","IMPRINT",EDGE,{"derivedFrom":sQuery(id+"F38.wireOp",EDGE,"E80.bottom")}),1.0]])]});
            extrude(context, id + "F39", {"entities" : qUnion([Q0]), "depth" : 800 * mm, "offsetDistance" : 25 * mm});
        }
        {
            var Q0;
            Q0=makeQuery(id+"F39.opExtrude","SWEPT_FACE",FACE,{"disambiguationData":[OSD([sQuery(id+"F38.wireOp",EDGE,"E80.left")])]});
            var sketch = newSketch(context, id + "F40", { "sketchPlane" : qUnion([Q0])});
            skLineSegment(sketch, "E81.bottom", {"start": v(-660, 75.87) * mm, "end": v(-840, 75.87) * mm});
            skLineSegment(sketch, "E81.top", {"start": v(-660, 220.87) * mm, "end": v(-840, 220.87) * mm});
            skLineSegment(sketch, "E81.left", {"start": v(-660, 75.87) * mm, "end": v(-660, 220.87) * mm});
            skLineSegment(sketch, "E81.right", {"start": v(-840, 75.87) * mm, "end": v(-840, 220.87) * mm});
            skLineSegment(sketch, "E82.0.1.0", {"start": v(-660, 375.87) * mm, "end": v(-840, 375.87) * mm});
            skLineSegment(sketch, "E82.0.1.1", {"start": v(-660, 230.87) * mm, "end": v(-840, 230.87) * mm});
            skLineSegment(sketch, "E82.0.1.2", {"start": v(-660, 230.87) * mm, "end": v(-660, 375.87) * mm});
            skLineSegment(sketch, "E82.0.1.3", {"start": v(-840, 230.87) * mm, "end": v(-840, 375.87) * mm});
            skLineSegment(sketch, "E82.0.2.0", {"start": v(-660, 530.87) * mm, "end": v(-840, 530.87) * mm});
            skLineSegment(sketch, "E82.0.2.1", {"start": v(-660, 385.87) * mm, "end": v(-840, 385.87) * mm});
            skLineSegment(sketch, "E82.0.2.2", {"start": v(-660, 385.87) * mm, "end": v(-660, 530.87) * mm});
            skLineSegment(sketch, "E82.0.2.3", {"start": v(-840, 385.87) * mm, "end": v(-840, 530.87) * mm});
            skLineSegment(sketch, "E82.0.3.0", {"start": v(-660, 685.87) * mm, "end": v(-840, 685.87) * mm});
            skLineSegment(sketch, "E82.0.3.1", {"start": v(-660, 540.87) * mm, "end": v(-840, 540.87) * mm});
            skLineSegment(sketch, "E82.0.3.2", {"start": v(-660, 540.87) * mm, "end": v(-660, 685.87) * mm});
            skLineSegment(sketch, "E82.0.3.3", {"start": v(-840, 540.87) * mm, "end": v(-840, 685.87) * mm});
            skLineSegment(sketch, "E82.0.4.0", {"start": v(-660, 840.87) * mm, "end": v(-840, 840.87) * mm});
            skLineSegment(sketch, "E82.0.4.1", {"start": v(-660, 695.87) * mm, "end": v(-840, 695.87) * mm});
            skLineSegment(sketch, "E82.0.4.2", {"start": v(-660, 695.87) * mm, "end": v(-660, 840.87) * mm});
            skLineSegment(sketch, "E82.0.4.3", {"start": v(-840, 695.87) * mm, "end": v(-840, 840.87) * mm});
            skLineSegment(sketch, "E82.direction1", {"start": v(-840, 75.87) * mm, "end": v(-815, 75.87) * mm, "construction": true});
            skLineSegment(sketch, "E82.direction2", {"start": v(-840, 75.87) * mm, "end": v(-840, 230.87) * mm, "construction": true});
            skSolve(sketch);
        }
        {
            var Q0;
            Q0 = qSketchRegion(id + "F40", true);
            extrude(context, id + "F41", {"entities" : qUnion([Q0]), "operationType" : NewBodyOperationType.REMOVE, "oppositeDirection" : true, "depth" : 590 * mm, "offsetDistance" : 25 * mm});
        }
        {
            var Q0;
            Q0=makeQuery(id+"F1.opExtrude","CAP_FACE",FACE,{"disambiguationData":[OSD([sQuery(id+"F0.wireOp",EDGE,"E0.bottom"),sQuery(id+"F0.wireOp",EDGE,"E0.top"),sQuery(id+"F0.wireOp",EDGE,"E0.left"),sQuery(id+"F0.wireOp",EDGE,"E0.right")])],"isStart":false});
            var sketch = newSketch(context, id + "F42", { "sketchPlane" : qUnion([Q0])});
            skLineSegment(sketch, "E83.bottom", {"start": v(0, 0) * mm, "end": v(60, 0) * mm});
            skLineSegment(sketch, "E83.top", {"start": v(0, 650) * mm, "end": v(60, 650) * mm});
            skLineSegment(sketch, "E83.left", {"start": v(0, 0) * mm, "end": v(0, 650) * mm});
            skLineSegment(sketch, "E83.right", {"start": v(60, 0) * mm, "end": v(60, 650) * mm});
            skSolve(sketch);
        }
        {
            var Q0;
            Q0 = qSketchRegion(id + "F42", true);
            extrude(context, id + "F43", {"entities" : qUnion([Q0]), "depth" : 870 * mm, "offsetDistance" : 25 * mm});
        }
        {
            var Q0;
            Q0=makeQuery(id+"F43.opExtrude","SWEPT_FACE",FACE,{"disambiguationData":[OSD([sQuery(id+"F42.wireOp",EDGE,"E83.right")])]});
            var sketch = newSketch(context, id + "F44", { "sketchPlane" : qUnion([Q0])});
            skLineSegment(sketch, "E84.bottom", {"start": v(80, 880) * mm, "end": v(570, 880) * mm});
            skLineSegment(sketch, "E84.top", {"start": v(80, 110) * mm, "end": v(570, 110) * mm});
            skLineSegment(sketch, "E84.left", {"start": v(50, 850) * mm, "end": v(50, 140) * mm});
            skLineSegment(sketch, "E84.right", {"start": v(600, 850) * mm, "end": v(600, 140) * mm});
            skPoint(sketch, "E85.visualSharp", {"position": v(50, 880) * mm});
            skArc(sketch, "E85.filletArc", {"start": v(80, 880) * mm, "mid": v(58.79, 871.21) * mm, "end": v(50, 850) * mm});
            skPoint(sketch, "E86.visualSharp", {"position": v(600, 880) * mm});
            skArc(sketch, "E86.filletArc", {"start": v(600, 850) * mm, "mid": v(591.21, 871.21) * mm, "end": v(570, 880) * mm});
            skPoint(sketch, "E87.visualSharp", {"position": v(600, 110) * mm});
            skArc(sketch, "E87.filletArc", {"start": v(570, 110) * mm, "mid": v(591.21, 118.79) * mm, "end": v(600, 140) * mm});
            skPoint(sketch, "E88.visualSharp", {"position": v(50, 110) * mm});
            skArc(sketch, "E88.filletArc", {"start": v(50, 140) * mm, "mid": v(58.79, 118.79) * mm, "end": v(80, 110) * mm});
            skSolve(sketch);
        }
        {
            var Q0;
            Q0=makeQuery(id+"F44.imprint","IMPRINT",FACE,{"disambiguationData":[TD([[makeQuery(id+"F44.imprint","IMPRINT",EDGE,{"derivedFrom":sQuery(id+"F44.wireOp",EDGE,"E84.bottom")}),-1.0]])]});
            extrude(context, id + "F45", {"entities" : qUnion([Q0]), "operationType" : NewBodyOperationType.REMOVE, "oppositeDirection" : true, "depth" : 30 * mm, "offsetDistance" : 25 * mm});
        }
        {
            var Q0;
            Q0 = qSketchRegion(id + "F44", true);
            extrude(context, id + "F46", {"entities" : qUnion([Q0]), "oppositeDirection" : true, "depth" : 30 * mm, "offsetDistance" : 25 * mm});
        }
        {
            var Q0;
            Q0=makeQuery(id+"F43.opExtrude","SWEPT_BODY",BODY,{"disambiguationData":[OSD([sQuery(id+"F42.wireOp",EDGE,"E83.bottom"),sQuery(id+"F42.wireOp",EDGE,"E83.top"),sQuery(id+"F42.wireOp",EDGE,"E83.left"),sQuery(id+"F42.wireOp",EDGE,"E83.right")])]});
            transform(context, id + "F47", {"entities" : qUnion([Q0]), "transformType" : TransformType.TRANSLATION_3D, "dx" : 0 * mm, "dy" : 850 * mm, "dz" : 0 * mm, "makeCopy" : true});
        }
        {
            var Q0;
            Q0=makeQuery(id+"F46.opExtrude","SWEPT_BODY",BODY,{"disambiguationData":[OSD([sQuery(id+"F44.wireOp",EDGE,"E84.bottom"),sQuery(id+"F44.wireOp",EDGE,"E84.top"),sQuery(id+"F44.wireOp",EDGE,"E84.left"),sQuery(id+"F44.wireOp",EDGE,"E84.right"),sQuery(id+"F44.wireOp",EDGE,"E85.filletArc"),sQuery(id+"F44.wireOp",EDGE,"E86.filletArc"),sQuery(id+"F44.wireOp",EDGE,"E87.filletArc"),sQuery(id+"F44.wireOp",EDGE,"E88.filletArc")])]});
            transform(context, id + "F48", {"entities" : qUnion([Q0]), "transformType" : TransformType.TRANSLATION_3D, "dx" : 0 * mm, "dy" : 850 * mm, "dz" : 0 * mm, "makeCopy" : true});
        }
        {
            var Q0;
            Q0=makeQuery(id+"F31.opExtrude","CAP_FACE",FACE,{"disambiguationData":[OSD([sQuery(id+"F30.wireOp",EDGE,"E68.bottom"),sQuery(id+"F30.wireOp",EDGE,"E68.top"),sQuery(id+"F30.wireOp",EDGE,"E68.left"),sQuery(id+"F30.wireOp",EDGE,"E68.right")])],"isStart":true});
            var sketch = newSketch(context, id + "F49", { "sketchPlane" : qUnion([Q0])});
            skLineSegment(sketch, "E89.bottom", {"start": v(4319, -1519) * mm, "end": v(1519, -1519) * mm});
            skLineSegment(sketch, "E89.top", {"start": v(4319, -831) * mm, "end": v(1519, -831) * mm});
            skLineSegment(sketch, "E89.left", {"start": v(4319, -1519) * mm, "end": v(4319, -831) * mm});
            skLineSegment(sketch, "E89.right", {"start": v(1519, -1519) * mm, "end": v(1519, -831) * mm});
            skSolve(sketch);
        }
        {
            var Q0;
            Q0 = qSketchRegion(id + "F49", true);
            extrude(context, id + "F50", {"entities" : qUnion([Q0]), "depth" : 19 * mm, "offsetDistance" : 25 * mm});
        }
        {
            var Q0;
            Q0=makeQuery(id+"F31.opExtrude","CAP_FACE",FACE,{"disambiguationData":[OSD([sQuery(id+"F30.wireOp",EDGE,"E68.bottom"),sQuery(id+"F30.wireOp",EDGE,"E68.top"),sQuery(id+"F30.wireOp",EDGE,"E68.left"),sQuery(id+"F30.wireOp",EDGE,"E68.right")])],"isStart":true});
            var sketch = newSketch(context, id + "F51", { "sketchPlane" : qUnion([Q0])});
            skLineSegment(sketch, "E90.bottom", {"start": v(-19, -831) * mm, "end": v(1519, -831) * mm});
            skLineSegment(sketch, "E90.top", {"start": v(-19, -1519) * mm, "end": v(1519, -1519) * mm});
            skLineSegment(sketch, "E90.left", {"start": v(-19, -831) * mm, "end": v(-19, -1519) * mm});
            skLineSegment(sketch, "E90.right", {"start": v(1519, -831) * mm, "end": v(1519, -1519) * mm});
            skSolve(sketch);
        }
        {
            var Q0;
            Q0 = qSketchRegion(id + "F51", true);
            extrude(context, id + "F52", {"entities" : qUnion([Q0]), "depth" : 19 * mm, "offsetDistance" : 25 * mm});
        }
        {
            var Q0;
            Q0=makeQuery(id+"F31.opExtrude","SWEPT_FACE",FACE,{"disambiguationData":[OSD([sQuery(id+"F30.wireOp",EDGE,"E68.right")])]});
            var sketch = newSketch(context, id + "F53", { "sketchPlane" : qUnion([Q0])});
            skSolve(sketch);
        }
        {
            var Q0;
            {var subQ0=sQuery(id+"F30.wireOp",EDGE,"E68.right");Q0=makeQuery(id+"F53.imprint","IMPRINT",FACE,{"disambiguationData":[TD([[makeQuery(id+"F53.imprint","IMPRINT",EDGE,{"derivedFrom":makeQuery(id+"F31.opExtrude","CAP_EDGE",EDGE,{"disambiguationData":[OSD([subQ0])],"isStart":true})}),-1.0]])]});}
            var sketch = newSketch(context, id + "F54", { "sketchPlane" : qUnion([Q0])});
            skLineSegment(sketch, "E91.bottom", {"start": v(-850, 60) * mm, "end": v(-1500, 60) * mm});
            skLineSegment(sketch, "E91.top", {"start": v(-850, 0) * mm, "end": v(-1500, 0) * mm});
            skLineSegment(sketch, "E91.left", {"start": v(-850, 60) * mm, "end": v(-850, 0) * mm});
            skLineSegment(sketch, "E91.right", {"start": v(-1500, 60) * mm, "end": v(-1500, 0) * mm});
            skSolve(sketch);
        }
        {
            var Q0;
            Q0 = qSketchRegion(id + "F54", true);
            extrude(context, id + "F55", {"entities" : qUnion([Q0]), "depth" : 19 * mm, "offsetDistance" : 25 * mm});
        }
        {
            var Q0;
            Q0=makeQuery(id+"F43.opExtrude","SWEPT_FACE",FACE,{"disambiguationData":[OSD([sQuery(id+"F42.wireOp",EDGE,"E83.right")])]});
            var sketch = newSketch(context, id + "F56", { "sketchPlane" : qUnion([Q0])});
            skSolve(sketch);
        }
        {
            var Q0;
            {var subQ0=sQuery(id+"F42.wireOp",EDGE,"E83.right");Q0=makeQuery(id+"F56.imprint","IMPRINT",FACE,{"disambiguationData":[TD([[makeQuery(id+"F56.imprint","IMPRINT",EDGE,{"derivedFrom":makeQuery(id+"F43.opExtrude","CAP_EDGE",EDGE,{"disambiguationData":[OSD([subQ0])],"isStart":true})}),1.0]])]});}
            var sketch = newSketch(context, id + "F57", { "sketchPlane" : qUnion([Q0])});
            skLineSegment(sketch, "E92.bottom", {"start": v(0, 930) * mm, "end": v(650, 930) * mm});
            skLineSegment(sketch, "E92.top", {"start": v(0, 60) * mm, "end": v(650, 60) * mm});
            skLineSegment(sketch, "E92.left", {"start": v(0, 930) * mm, "end": v(0, 60) * mm});
            skLineSegment(sketch, "E92.right", {"start": v(650, 930) * mm, "end": v(650, 60) * mm});
            skSolve(sketch);
        }
        {
            var Q0;
            Q0 = qSketchRegion(id + "F57", true);
            extrude(context, id + "F58", {"entities" : qUnion([Q0]), "depth" : 3600 * mm, "offsetDistance" : 25 * mm});
        }
    });
